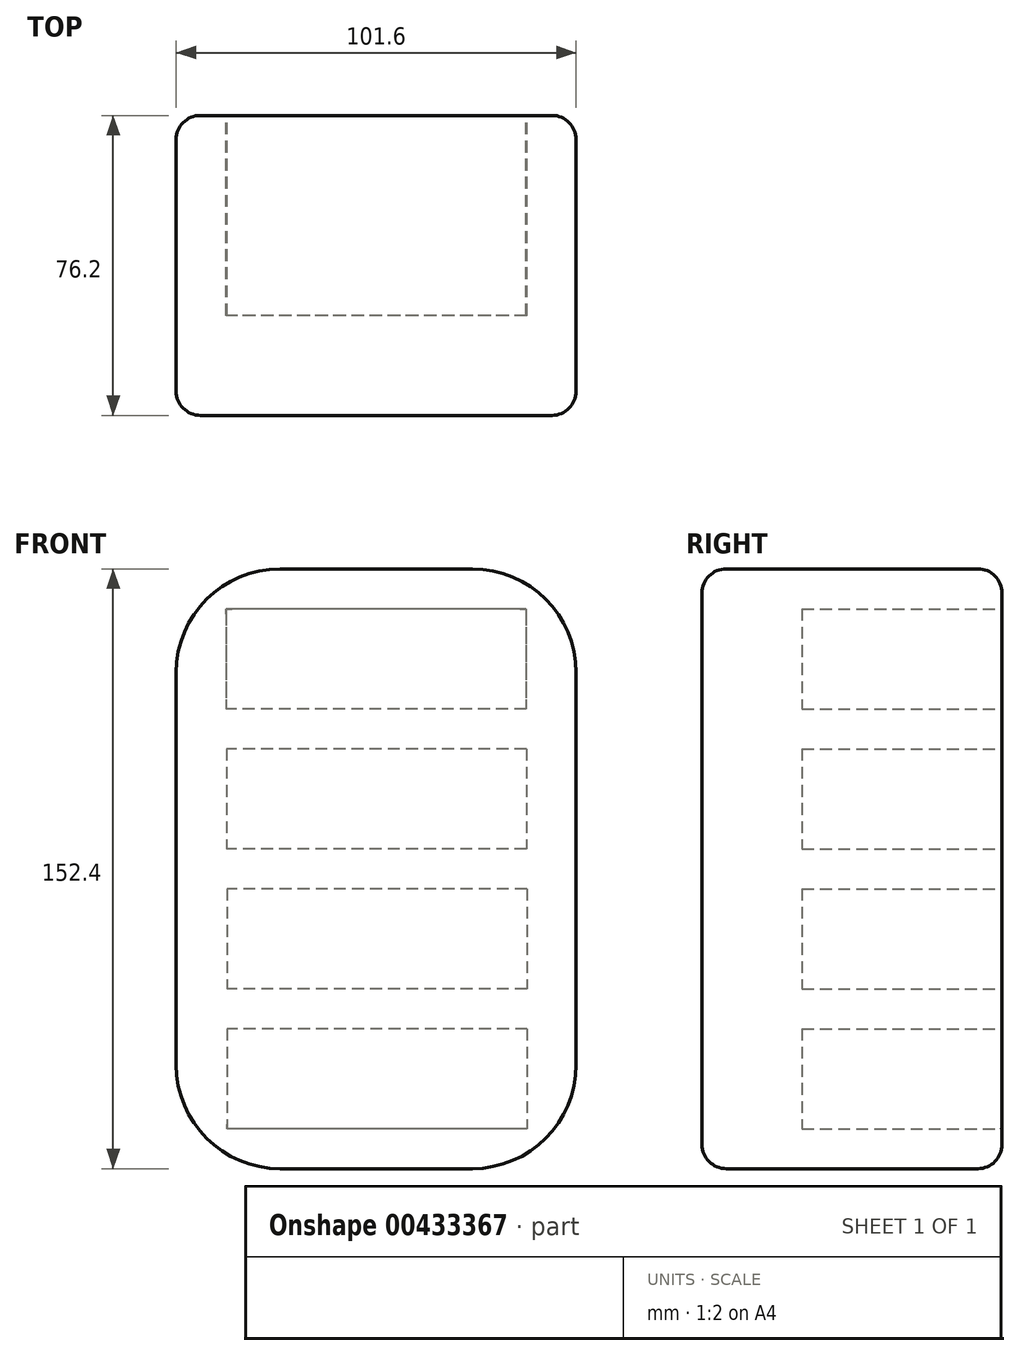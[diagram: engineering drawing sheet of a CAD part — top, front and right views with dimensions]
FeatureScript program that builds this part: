
annotation { "Feature Type Name" : "Feature", "Feature Type Description" : "" }
export const myFeature = defineFeature(function(context is Context, id is Id, definition is map)
    precondition{}
    {
        {
            var Q0;
            Q0=qCreatedBy(makeId("Top.planeOp"),FACE);
            var sketch = newSketch(context, id + "F0", { "sketchPlane" : qUnion([Q0])});
            skLineSegment(sketch, "E0.bottom", {"start": v(-51.4, 29.8) * mm, "end": v(50.2, 29.8) * mm});
            skLineSegment(sketch, "E0.top", {"start": v(-51.4, -46.4) * mm, "end": v(50.2, -46.4) * mm});
            skLineSegment(sketch, "E0.left", {"start": v(-51.4, 29.8) * mm, "end": v(-51.4, -46.4) * mm});
            skLineSegment(sketch, "E0.right", {"start": v(50.2, 29.8) * mm, "end": v(50.2, -46.4) * mm});
            skSolve(sketch);
        }
        {
            var Q0;
            Q0 = qSketchRegion(id + "F0", true);
            extrude(context, id + "F1", {"entities" : qUnion([Q0]), "depth" : 152.4 * mm});
        }
        {
            var Q0;
            Q0=makeQuery(id+"F1.opExtrude","SWEPT_FACE",FACE,{"disambiguationData":[OSD([sQuery(id+"F0.wireOp",EDGE,"E0.bottom")])]});
            var sketch = newSketch(context, id + "F2", { "sketchPlane" : qUnion([Q0])});
            skLineSegment(sketch, "E1.bottom", {"start": v(-37.5, 142.24) * mm, "end": v(38.7, 142.24) * mm});
            skLineSegment(sketch, "E1.top", {"start": v(-37.5, 116.84) * mm, "end": v(38.7, 116.84) * mm});
            skLineSegment(sketch, "E1.left", {"start": v(-37.5, 142.24) * mm, "end": v(-37.5, 116.84) * mm});
            skLineSegment(sketch, "E1.right", {"start": v(38.7, 142.24) * mm, "end": v(38.7, 116.84) * mm});
            skLineSegment(sketch, "E2.0.1.0", {"start": v(-37.6, 106.68) * mm, "end": v(-37.6, 81.28) * mm});
            skLineSegment(sketch, "E2.0.1.1", {"start": v(-37.6, 106.68) * mm, "end": v(38.6, 106.68) * mm});
            skLineSegment(sketch, "E2.0.1.2", {"start": v(-37.6, 81.28) * mm, "end": v(38.6, 81.28) * mm});
            skLineSegment(sketch, "E2.0.1.3", {"start": v(38.6, 106.68) * mm, "end": v(38.6, 81.28) * mm});
            skLineSegment(sketch, "E2.0.2.0", {"start": v(-37.68, 71.12) * mm, "end": v(-37.68, 45.72) * mm});
            skLineSegment(sketch, "E2.0.2.1", {"start": v(-37.68, 71.12) * mm, "end": v(38.52, 71.12) * mm});
            skLineSegment(sketch, "E2.0.2.2", {"start": v(-37.68, 45.72) * mm, "end": v(38.52, 45.72) * mm});
            skLineSegment(sketch, "E2.0.2.3", {"start": v(38.52, 71.12) * mm, "end": v(38.52, 45.72) * mm});
            skLineSegment(sketch, "E2.0.3.0", {"start": v(-37.76, 35.56) * mm, "end": v(-37.76, 10.16) * mm});
            skLineSegment(sketch, "E2.0.3.1", {"start": v(-37.76, 35.56) * mm, "end": v(38.44, 35.56) * mm});
            skLineSegment(sketch, "E2.0.3.2", {"start": v(-37.76, 10.16) * mm, "end": v(38.44, 10.16) * mm});
            skLineSegment(sketch, "E2.0.3.3", {"start": v(38.44, 35.56) * mm, "end": v(38.44, 10.16) * mm});
            skLineSegment(sketch, "E2.direction1", {"start": v(-37.5, 116.84) * mm, "end": v(-12.1, 116.84) * mm, "construction": true});
            skLineSegment(sketch, "E2.direction2", {"start": v(-37.5, 116.84) * mm, "end": v(-37.6, 81.28) * mm, "construction": true});
            skSolve(sketch);
        }
        {
            var Q0;
            Q0 = qSketchRegion(id + "F2", true);
            extrude(context, id + "F3", {"entities" : qUnion([Q0]), "operationType" : NewBodyOperationType.REMOVE, "oppositeDirection" : true, "depth" : 50.8 * mm});
        }
        {
            var Q0;
            Q0=makeQuery(id+"F1.opExtrude","CAP_EDGE",EDGE,{"disambiguationData":[OSD([sQuery(id+"F0.wireOp",EDGE,"E0.left")])],"isStart":false});
            var Q1;
            Q1=makeQuery(id+"F1.opExtrude","CAP_EDGE",EDGE,{"disambiguationData":[OSD([sQuery(id+"F0.wireOp",EDGE,"E0.right")])],"isStart":false});
            var Q2;
            Q2=makeQuery(id+"F1.opExtrude","CAP_EDGE",EDGE,{"disambiguationData":[OSD([sQuery(id+"F0.wireOp",EDGE,"E0.left")])],"isStart":true});
            var Q3;
            Q3=makeQuery(id+"F1.opExtrude","CAP_EDGE",EDGE,{"disambiguationData":[OSD([sQuery(id+"F0.wireOp",EDGE,"E0.right")])],"isStart":true});
            fillet(context, id + "F4", {"entities" : qUnion([Q0, Q1, Q2, Q3]), "radius" : 26.37 * mm, "tangentPropagation" : true, "allowEdgeOverflow" : false});
        }
        {
            var Q0;
            Q0=makeQuery(id+"F1.opExtrude","CAP_EDGE",EDGE,{"disambiguationData":[OSD([sQuery(id+"F0.wireOp",EDGE,"E0.bottom")])],"isStart":false});
            var Q1;
            Q1=makeQuery(id+"F1.opExtrude","CAP_EDGE",EDGE,{"disambiguationData":[OSD([sQuery(id+"F0.wireOp",EDGE,"E0.top")])],"isStart":false});
            var Q2;
            Q2=makeQuery(id+"F1.opExtrude","CAP_EDGE",EDGE,{"disambiguationData":[OSD([sQuery(id+"F0.wireOp",EDGE,"E0.bottom")])],"isStart":true});
            var Q3;
            Q3=makeQuery(id+"F1.opExtrude","CAP_EDGE",EDGE,{"disambiguationData":[OSD([sQuery(id+"F0.wireOp",EDGE,"E0.top")])],"isStart":true});
            fillet(context, id + "F5", {"entities" : qUnion([Q0, Q1, Q2, Q3]), "radius" : 6.13 * mm, "tangentPropagation" : true, "allowEdgeOverflow" : false});
        }
    });
